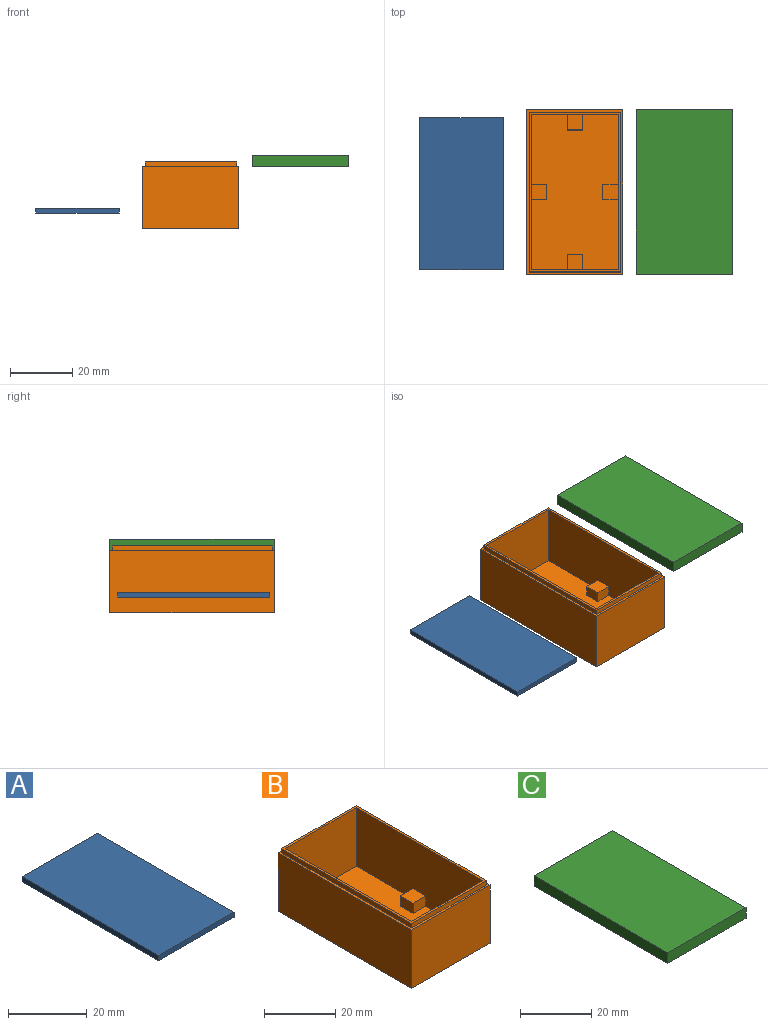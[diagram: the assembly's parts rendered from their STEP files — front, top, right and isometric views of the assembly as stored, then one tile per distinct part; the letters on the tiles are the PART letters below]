
ASSEMBLY  parts=3 mates=4
PART A: 6 faces, bbox 27x49x1.6 mm
  f0: plane 27x1.6mm, normal (0,1,0), area 43.2mm2, adj f1,f3,f4,f5
  f1: plane 49x1.6mm, normal (-1,0,0), area 78.4mm2, adj f0,f2,f4,f5
  f2: plane 27x1.6mm, normal (0,-1,0), area 43.2mm2, adj f1,f3,f4,f5
  f3: plane 49x1.6mm, normal (1,0,0), area 78.4mm2, adj f0,f2,f4,f5
  f4: plane 49x27mm, normal (0,0,1), area 1323mm2, adj f0,f1,f2,f3
  f5: plane 49x27mm, normal (0,0,-1), area 1323mm2, adj f0,f1,f2,f3
PART B: 32 faces, bbox 31x53x21.5 mm
  f0: plane 50x20mm, normal (-1,0,0), area 982.5mm2, adj f1,f2,f16,f18,f19,f20,f25
  f1: plane 28x20mm, normal (0,-1,0), area 542.5mm2, adj f0,f3,f12,f14,f15,f20,f25
  f2: plane 28x20mm, normal (0,1,0), area 542.5mm2, adj f0,f3,f5,f6,f7,f20,f25
  f3: plane 50x20mm, normal (1,0,0), area 982.5mm2, adj f1,f2,f9,f10,f11,f20,f25
  f4: plane 5x3.5mm, normal (0,1,0), area 17.5mm2, adj f5,f6,f7,f20
  f5: plane 5x3.5mm, normal (-1,0,0), area 17.5mm2, adj f2,f4,f7,f20
  f6: plane 5x3.5mm, normal (1,0,0), area 17.5mm2, adj f2,f4,f7,f20
  f7: plane 5x5mm, normal (0,0,1), area 25mm2, adj f2,f4,f5,f6
  f8: plane 5x3.5mm, normal (1,0,0), area 17.5mm2, adj f9,f10,f11,f20
  f9: plane 5x3.5mm, normal (0,1,0), area 17.5mm2, adj f3,f8,f11,f20
  f10: plane 5x3.5mm, normal (0,-1,0), area 17.5mm2, adj f3,f8,f11,f20
  f11: plane 5x5mm, normal (0,0,1), area 25mm2, adj f3,f8,f9,f10
  f12: plane 5x3.5mm, normal (-1,0,0), area 17.5mm2, adj f1,f13,f15,f20
  f13: plane 5x3.5mm, normal (0,-1,0), area 17.5mm2, adj f12,f14,f15,f20
  f14: plane 5x3.5mm, normal (1,0,0), area 17.5mm2, adj f1,f13,f15,f20
  f15: plane 5x5mm, normal (0,0,1), area 25mm2, adj f1,f12,f13,f14
  f16: plane 5x3.5mm, normal (0,1,0), area 17.5mm2, adj f0,f17,f19,f20
  f17: plane 5x3.5mm, normal (-1,0,0), area 17.5mm2, adj f16,f18,f19,f20
  f18: plane 5x3.5mm, normal (0,-1,0), area 17.5mm2, adj f0,f17,f19,f20
  f19: plane 5x5mm, normal (0,0,1), area 25mm2, adj f0,f16,f17,f18
  f20: plane 50x28mm, normal (0,0,1), area 1300mm2, adj f0,f1,f2,f3,f4,f5,f6,f8
  f21: plane 29.5x1.5mm, normal (0,1,0), area 44.2mm2, adj f22,f24,f25,f31
  f22: plane 51.5x1.5mm, normal (-1,0,0), area 77.2mm2, adj f21,f23,f25,f31
  f23: plane 29.5x1.5mm, normal (0,-1,0), area 44.2mm2, adj f22,f24,f25,f31
  f24: plane 51.5x1.5mm, normal (1,0,0), area 77.2mm2, adj f21,f23,f25,f31
  f25: plane 51.5x29.5mm, normal (0,0,1), area 119.3mm2, adj f0,f1,f2,f3,f21,f22,f23,f24
  f26: plane 53x31mm, normal (0,0,-1), area 1643mm2, adj f27,f28,f29,f30
  f27: plane 53x20mm, normal (1,0,0), area 1060mm2, adj f26,f28,f30,f31
  f28: plane 31x20mm, normal (0,-1,0), area 620mm2, adj f26,f27,f29,f31
  f29: plane 53x20mm, normal (-1,0,0), area 1060mm2, adj f26,f28,f30,f31
  f30: plane 31x20mm, normal (0,1,0), area 620mm2, adj f26,f27,f29,f31
  f31: plane 53x31mm, normal (0,0,1), area 123.7mm2, adj f21,f22,f23,f24,f27,f28,f29,f30
PART C: 11 faces, bbox 31x53x3.6 mm
  f0: plane 51.6x1.6mm, normal (-1,0,0), area 82.6mm2, adj f1,f7,f8,f9
  f1: plane 29.6x1.6mm, normal (0,1,0), area 47.4mm2, adj f0,f2,f8,f9
  f2: plane 51.6x1.6mm, normal (1,0,0), area 82.6mm2, adj f1,f7,f8,f9
  f3: plane 53x3.6mm, normal (-1,0,0), area 190.8mm2, adj f4,f6,f8,f10
  f4: plane 31x3.6mm, normal (0,-1,0), area 111.6mm2, adj f3,f5,f8,f10
  f5: plane 53x3.6mm, normal (1,0,0), area 190.8mm2, adj f4,f6,f8,f10
  f6: plane 31x3.6mm, normal (0,1,0), area 111.6mm2, adj f3,f5,f8,f10
  f7: plane 29.6x1.6mm, normal (0,-1,0), area 47.4mm2, adj f0,f2,f8,f9
  f8: plane 53x31mm, normal (0,0,-1), area 115.6mm2, adj f0,f1,f2,f3,f4,f5,f6,f7
  f9: plane 51.6x29.6mm, normal (0,0,-1), area 1527.4mm2, adj f0,f1,f2,f7
  f10: plane 53x31mm, normal (0,0,1), area 1643mm2, adj f3,f4,f5,f6
PLACE A t=(-14.51,-1.04,55.57)mm
PLACE B t=(-28.1,-12.18,50.57)mm
PLACE C t=(19.91,-4.62,25.57)mm
MATE planar C.f1 <-> B.f23  axis (0,1,0) through (-26.44,-55.98,71.37)mm
MATE planar A.f2 <-> B.f2  axis (0,-1,0) through (-98.16,-55.23,56.37)mm
MATE planar C.f8 <-> B.f31  axis (0,0,-1) through (-26.44,-30.18,70.57)mm
MATE planar A.f5 <-> B.f11  axis (0,0,-1) through (-98.16,-30.73,55.57)mm
